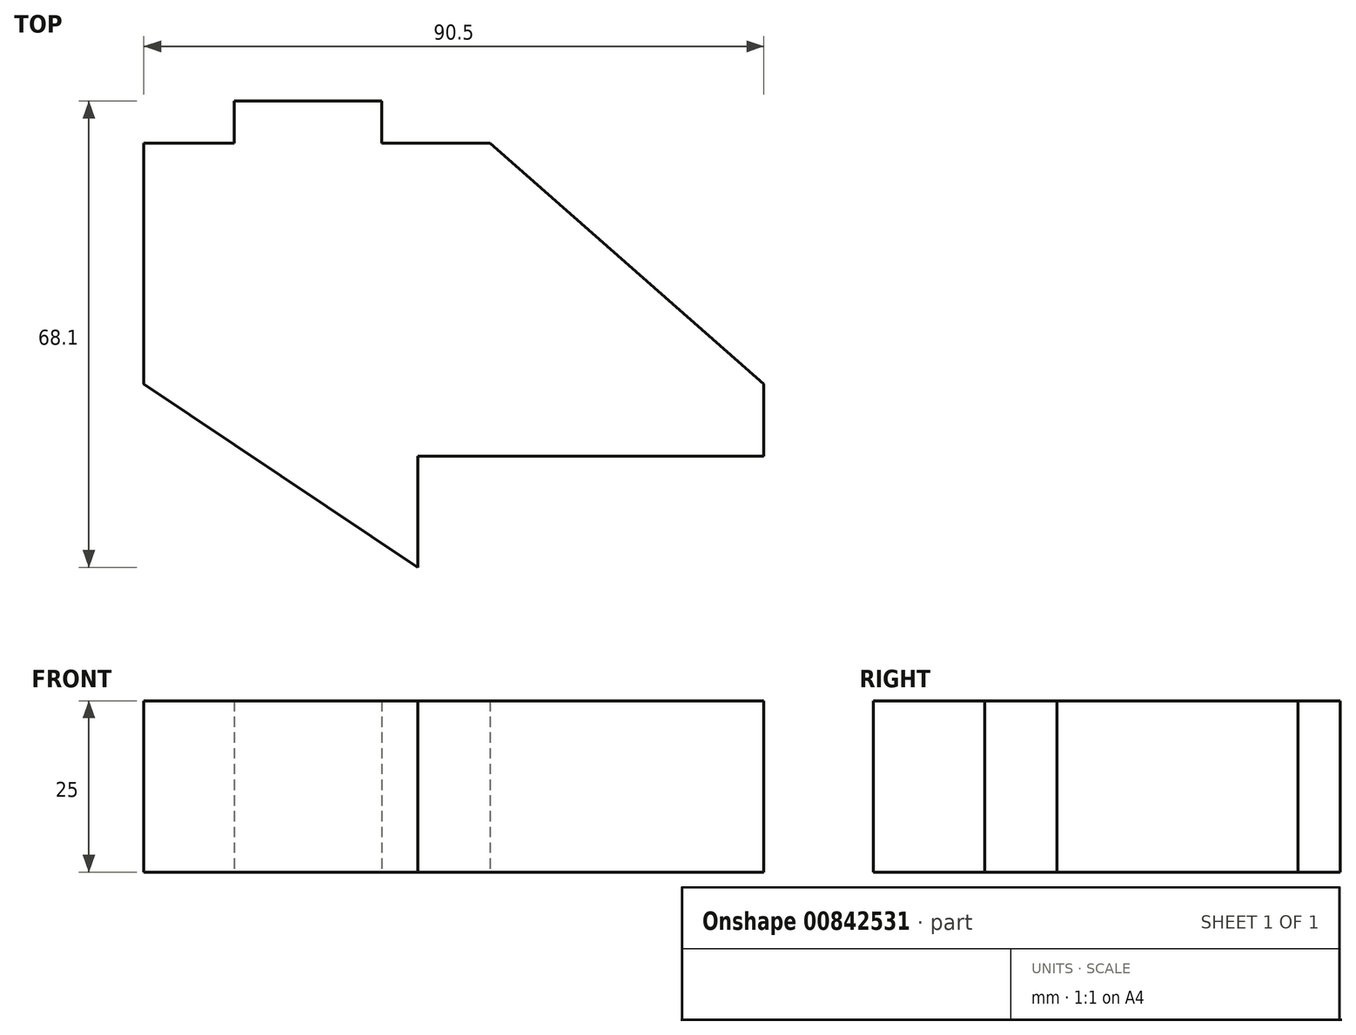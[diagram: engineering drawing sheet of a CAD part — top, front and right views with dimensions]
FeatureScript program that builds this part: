
annotation { "Feature Type Name" : "Feature", "Feature Type Description" : "" }
export const myFeature = defineFeature(function(context is Context, id is Id, definition is map)
    precondition{}
    {
        {
            var Q0;
            Q0=qCreatedBy(makeId("Top.planeOp"),FACE);
            var sketch = newSketch(context, id + "F0", { "sketchPlane" : qUnion([Q0])});
            skLineSegment(sketch, "E0", {"start": v(-44.62, 31.85) * mm, "end": v(-31.44, 31.85) * mm});
            skLineSegment(sketch, "E1", {"start": v(-31.44, 31.85) * mm, "end": v(-31.44, 38) * mm});
            skLineSegment(sketch, "E2", {"start": v(-31.44, 38) * mm, "end": v(-9.91, 38) * mm});
            skLineSegment(sketch, "E3", {"start": v(-9.91, 38) * mm, "end": v(-9.91, 31.85) * mm});
            skLineSegment(sketch, "E4", {"start": v(-9.91, 31.85) * mm, "end": v(5.9, 31.85) * mm});
            skLineSegment(sketch, "E5", {"start": v(5.9, 31.85) * mm, "end": v(45.88, -3.3) * mm});
            skLineSegment(sketch, "E6", {"start": v(-44.62, 31.85) * mm, "end": v(-4.64, -3.3) * mm});
            skLineSegment(sketch, "E7", {"start": v(-4.64, -3.3) * mm, "end": v(-4.64, -13.84) * mm});
            skLineSegment(sketch, "E8", {"start": v(-4.64, -13.84) * mm, "end": v(45.88, -13.84) * mm});
            skLineSegment(sketch, "E9", {"start": v(45.88, -13.84) * mm, "end": v(45.88, -3.3) * mm});
            skLineSegment(sketch, "E10", {"start": v(-44.62, 31.85) * mm, "end": v(-44.62, -3.3) * mm});
            skLineSegment(sketch, "E11", {"start": v(-44.62, -3.3) * mm, "end": v(5.46, -3.3) * mm});
            skLineSegment(sketch, "E12", {"start": v(5.46, -3.3) * mm, "end": v(5.9, 31.85) * mm});
            skLineSegment(sketch, "E13", {"start": v(5.02, 29.65) * mm, "end": v(5.9, 31.85) * mm});
            skLineSegment(sketch, "E14", {"start": v(-4.64, -13.84) * mm, "end": v(-4.64, -30.1) * mm});
            skLineSegment(sketch, "E15", {"start": v(-4.64, -30.1) * mm, "end": v(-44.62, -3.3) * mm});
            skLineSegment(sketch, "E16", {"start": v(-3.32, -30.1) * mm, "end": v(45.88, -29.22) * mm});
            skLineSegment(sketch, "E17", {"start": v(45.88, -29.22) * mm, "end": v(45.88, -13.84) * mm});
            skSolve(sketch);
        }
        {
            var Q0;
            Q0 = qSketchRegion(id + "F0", true);
            extrude(context, id + "F1", {"entities" : qUnion([Q0]), "depth" : 25 * mm, "offsetDistance" : 25 * mm});
        }
    });
